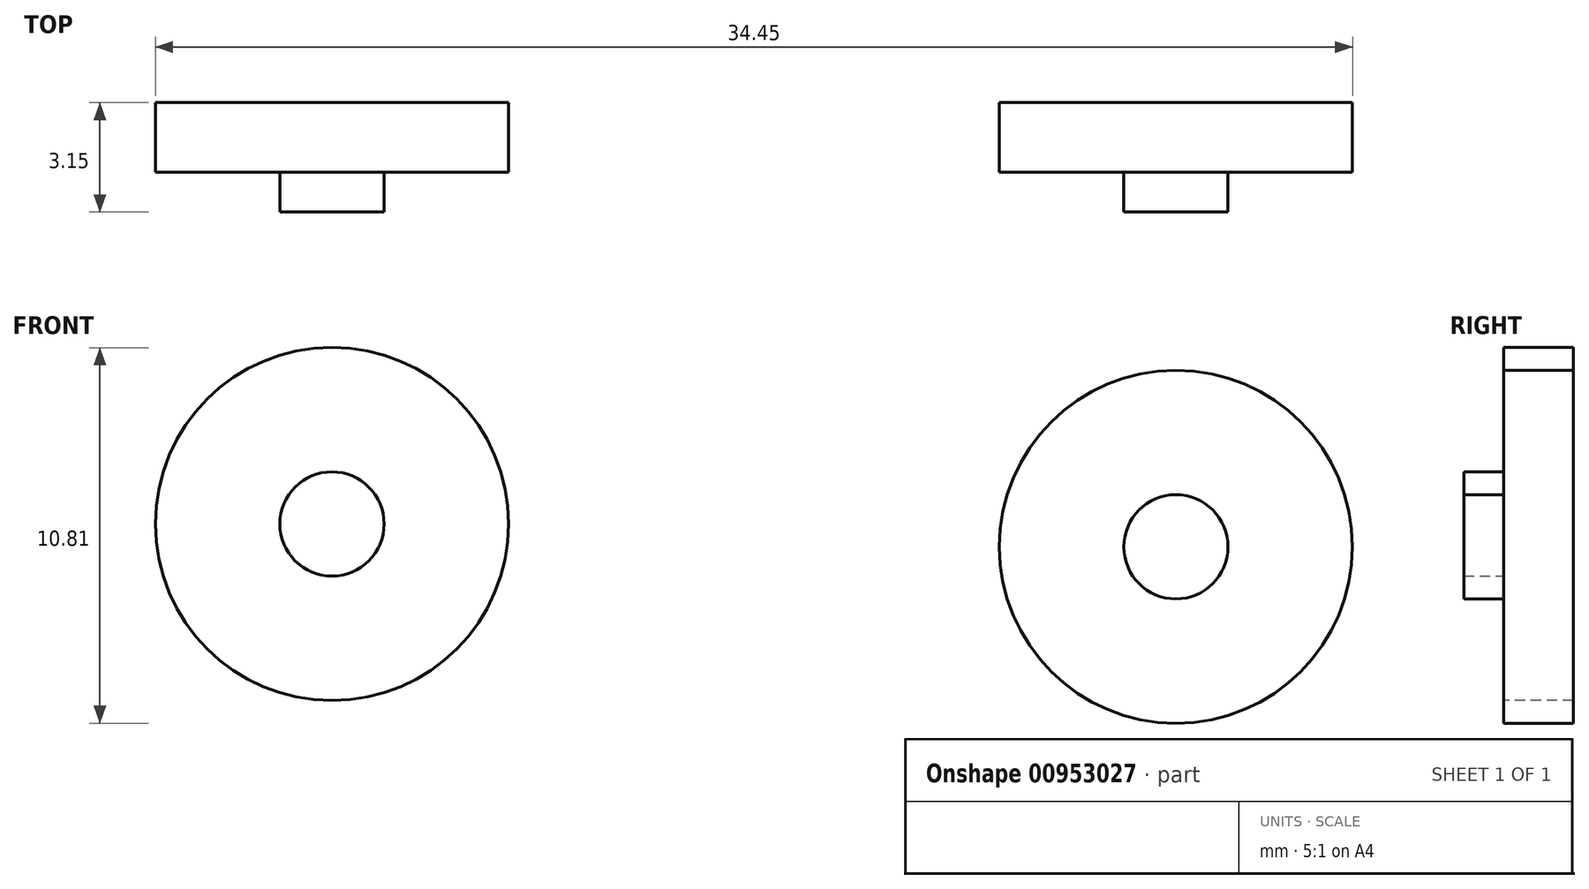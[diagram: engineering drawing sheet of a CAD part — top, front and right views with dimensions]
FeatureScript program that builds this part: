
annotation { "Feature Type Name" : "Feature", "Feature Type Description" : "" }
export const myFeature = defineFeature(function(context is Context, id is Id, definition is map)
    precondition{}
    {
        {
            var Q0;
            Q0=qCreatedBy(makeId("Front.planeOp"),FACE);
            var sketch = newSketch(context, id + "F0", { "sketchPlane" : qUnion([Q0])});
            skCircle(sketch, "E0", {"center": v(-55.31, 54.57) * mm, "radius": 5.08 * mm});
            skCircle(sketch, "E1", {"center": v(-31.02, 53.92) * mm, "radius": 5.08 * mm});
            skSolve(sketch);
        }
        {
            var Q0;
            Q0=makeQuery(id+"F0.imprint","IMPRINT",FACE,{"disambiguationData":[TD([[makeQuery(id+"F0.imprint","IMPRINT",EDGE,{"derivedFrom":sQuery(id+"F0.wireOp",EDGE,"E1")}),1.0]])]});
            var Q1;
            Q1=makeQuery(id+"F0.imprint","IMPRINT",FACE,{"disambiguationData":[TD([[makeQuery(id+"F0.imprint","IMPRINT",EDGE,{"derivedFrom":sQuery(id+"F0.wireOp",EDGE,"E0")}),1.0]])]});
            extrude(context, id + "F1", {"entities" : qUnion([Q0, Q1]), "depth" : -2 * mm, "offsetDistance" : 25.4 * mm});
        }
        {
            var Q0;
            Q0=makeQuery(id+"F1.opExtrude","CAP_FACE",FACE,{"disambiguationData":[OSD([sQuery(id+"F0.wireOp",EDGE,"E0")])],"isStart":true});
            var sketch = newSketch(context, id + "F2", { "sketchPlane" : qUnion([Q0])});
            skCircle(sketch, "E2", {"center": v(-55.31, 54.57) * mm, "radius": 1.5 * mm});
            skSolve(sketch);
        }
        {
            var Q0;
            Q0=makeQuery(id+"F1.opExtrude","CAP_FACE",FACE,{"disambiguationData":[OSD([sQuery(id+"F0.wireOp",EDGE,"E1")])],"isStart":true});
            var sketch = newSketch(context, id + "F3", { "sketchPlane" : qUnion([Q0])});
            skCircle(sketch, "E3", {"center": v(-31.02, 53.92) * mm, "radius": 1.5 * mm});
            skSolve(sketch);
        }
        {
            var Q0;
            Q0=makeQuery(id+"F3.imprint","IMPRINT",FACE,{"disambiguationData":[TD([[makeQuery(id+"F3.imprint","IMPRINT",EDGE,{"derivedFrom":sQuery(id+"F3.wireOp",EDGE,"E3")}),1.0]])]});
            var Q1;
            Q1=makeQuery(id+"F2.imprint","IMPRINT",FACE,{"disambiguationData":[TD([[makeQuery(id+"F2.imprint","IMPRINT",EDGE,{"derivedFrom":sQuery(id+"F2.wireOp",EDGE,"E2")}),1.0]])]});
            var Q2;
            Q2=sQuery(id+"F2.wireOp",EDGE,"E2");
            var Q3;
            Q3=sQuery(id+"F3.wireOp",EDGE,"E3");
            extrude(context, id + "F4", {"entities" : qUnion([Q0, Q1]), "surfaceEntities" : qUnion([Q2, Q3]), "depth" : 1.15 * mm, "offsetDistance" : 25.4 * mm});
        }
    });
